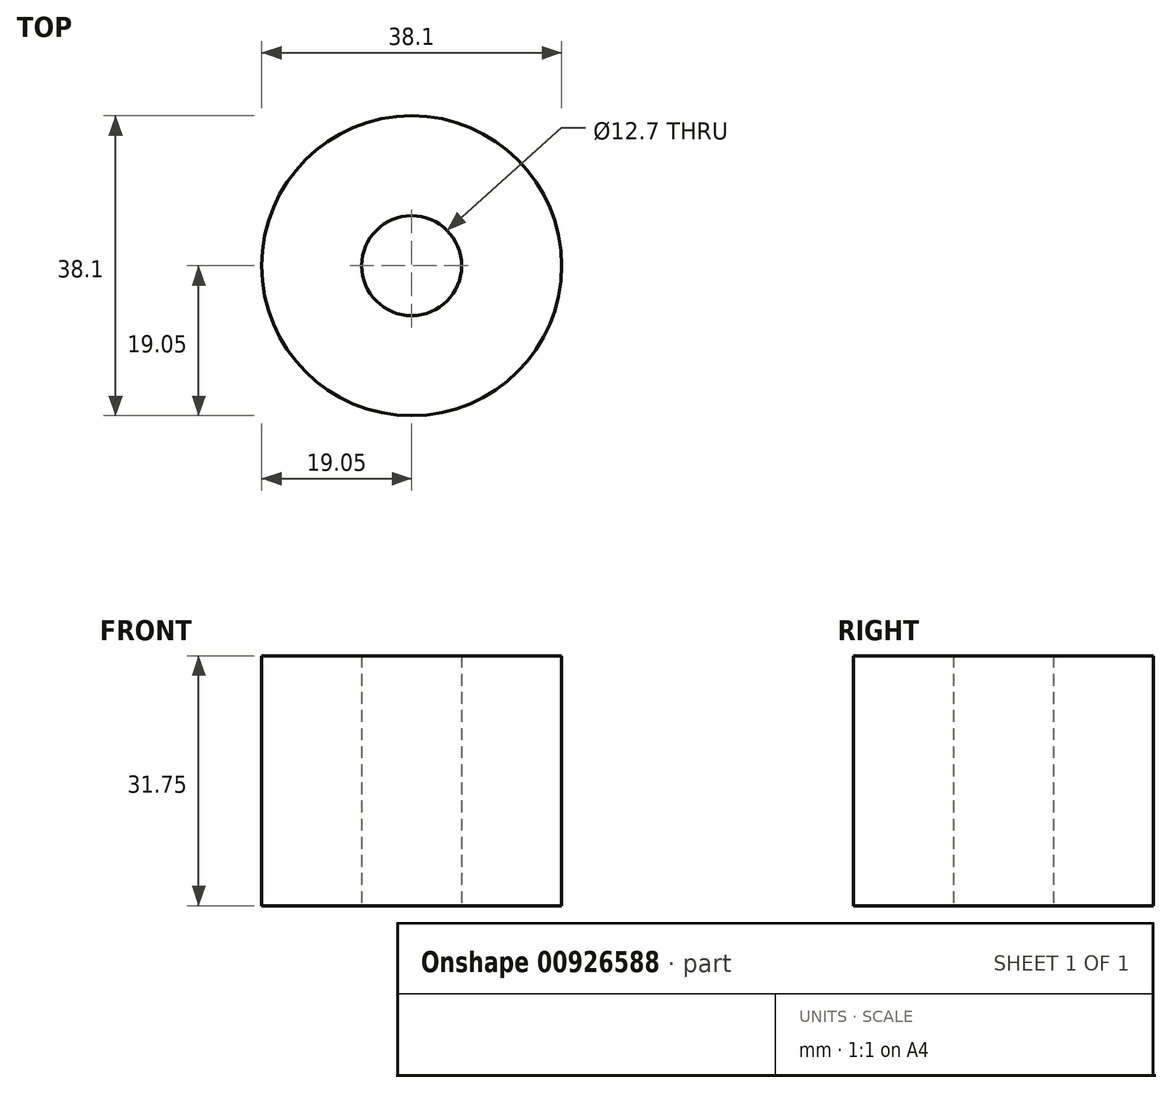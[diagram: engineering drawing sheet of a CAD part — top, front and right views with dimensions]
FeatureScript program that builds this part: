
annotation { "Feature Type Name" : "Feature", "Feature Type Description" : "" }
export const myFeature = defineFeature(function(context is Context, id is Id, definition is map)
    precondition{}
    {
        {
            var Q0;
            Q0=qCreatedBy(makeId("Top.planeOp"),FACE);
            var sketch = newSketch(context, id + "F0", { "sketchPlane" : qUnion([Q0])});
            skCircle(sketch, "E0", {"center": v(0, 0) * mm, "radius": 19.05 * mm});
            skCircle(sketch, "E1", {"center": v(0, 0) * mm, "radius": 6.35 * mm});
            skSolve(sketch);
        }
        {
            var Q0;
            Q0=makeQuery(id+"F0.imprint","IMPRINT",FACE,{"disambiguationData":[TD([[makeQuery(id+"F0.imprint","IMPRINT",EDGE,{"derivedFrom":sQuery(id+"F0.wireOp",EDGE,"E0")}),1.0]])]});
            extrude(context, id + "F1", {"entities" : qUnion([Q0]), "depth" : 31.75 * mm, "offsetDistance" : 25.4 * mm});
        }
    });
